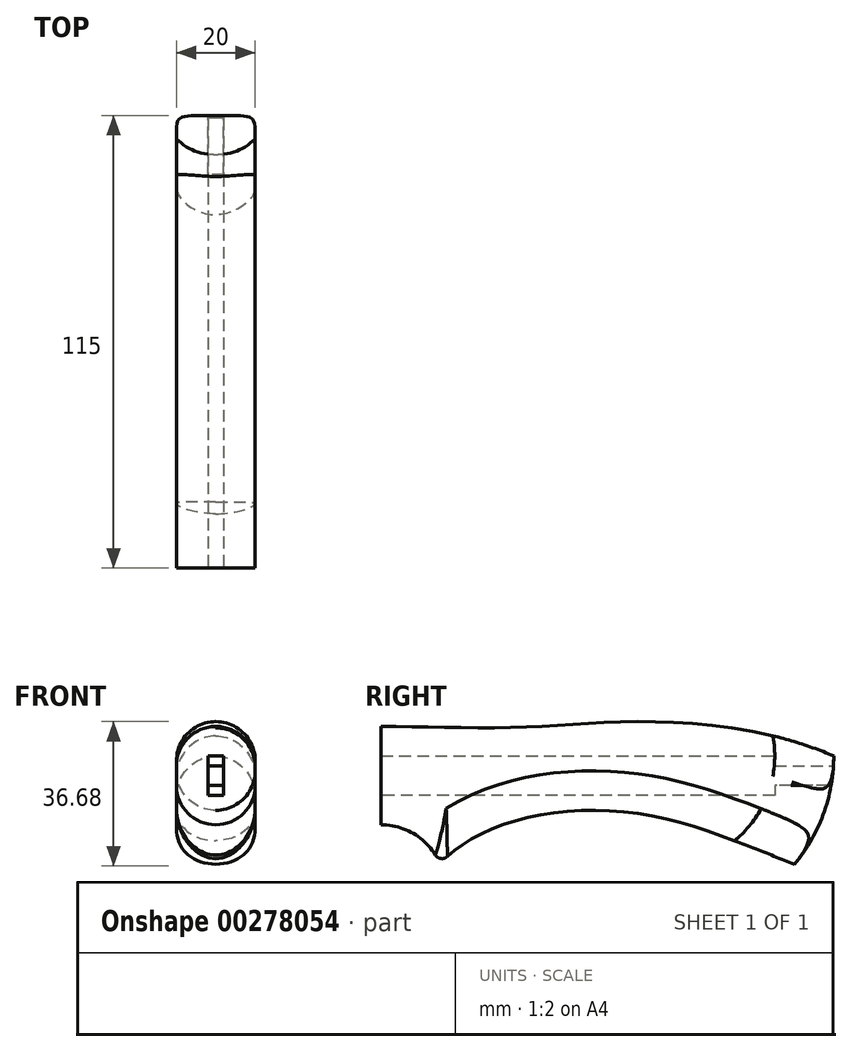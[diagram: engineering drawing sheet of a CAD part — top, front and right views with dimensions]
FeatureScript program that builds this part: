
annotation { "Feature Type Name" : "Feature", "Feature Type Description" : "" }
export const myFeature = defineFeature(function(context is Context, id is Id, definition is map)
    precondition{}
    {
        {
            var Q0;
            Q0=qCreatedBy(makeId("Right.planeOp"),FACE);
            var sketch = newSketch(context, id + "F0", { "sketchPlane" : qUnion([Q0])});
            skLineSegment(sketch, "E0", {"start": v(0, 0) * mm, "end": v(0, 5) * mm});
            skLineSegment(sketch, "E1", {"start": v(0, 5) * mm, "end": v(100, 5) * mm});
            skLineSegment(sketch, "E2", {"start": v(100, 5) * mm, "end": v(100, 2.5) * mm});
            skLineSegment(sketch, "E3", {"start": v(100, 2.5) * mm, "end": v(115, 2.5) * mm});
            skLineSegment(sketch, "E4", {"start": v(115, 2.5) * mm, "end": v(115, -2.5) * mm});
            skLineSegment(sketch, "E5", {"start": v(115, -2.5) * mm, "end": v(100, -2.5) * mm});
            skLineSegment(sketch, "E6", {"start": v(100, -2.5) * mm, "end": v(100, -5) * mm});
            skLineSegment(sketch, "E7", {"start": v(100, -5) * mm, "end": v(0, -5) * mm});
            skLineSegment(sketch, "E8", {"start": v(0, -5) * mm, "end": v(0, 0) * mm});
            skSolve(sketch);
        }
        {
            var Q0;
            Q0=qCreatedBy(makeId("Right.planeOp"),FACE);
            var sketch = newSketch(context, id + "F1", { "sketchPlane" : qUnion([Q0])});
            skLineSegment(sketch, "E9", {"start": v(0, 0) * mm, "end": v(0, 12.5) * mm});
            skLineSegment(sketch, "E10", {"start": v(0, 0) * mm, "end": v(0, -12.5) * mm});
            skLineSegment(sketch, "E11", {"start": v(0, -12.5) * mm, "end": v(-8.74, -12.5) * mm, "construction": true});
            skLineSegment(sketch, "E12", {"start": v(0, 12.5) * mm, "end": v(-9.37, 12.5) * mm, "construction": true});
            skFitSpline(sketch, "E13", {"points": [v(0, 12.5) * mm, v(33.17, 12.23) * mm, v(65.02, 13.71) * mm, v(115, 5) * mm], "startDerivative": vector(96.51, 0) * mm, "endDerivative": vector(135.83, -57.76) * mm});
            skArc(sketch, "E14", {"start": v(15, -22.5) * mm, "mid": v(9.01, -15.23) * mm, "end": v(0, -12.5) * mm});
            skArc(sketch, "E15", {"start": v(105, -22.5) * mm, "mid": v(112.42, -9.63) * mm, "end": v(115, 5) * mm});
            skLineSegment(sketch, "E16", {"start": v(115, 5) * mm, "end": v(115, 20.98) * mm, "construction": true});
            skFitSpline(sketch, "E17", {"points": [v(15, -22.5) * mm, v(32.94, -11.8) * mm, v(68.4, -10.16) * mm, v(105, -22.5) * mm], "startDerivative": vector(36.96, 44.62) * mm, "endDerivative": vector(92.76, -35.84) * mm});
            skArc(sketch, "E18", {"start": v(89.8, -16.52) * mm, "mid": v(98.31, -4.54) * mm, "end": v(99.53, 10.11) * mm});
            skSolve(sketch);
        }
        {
            var Q0;
            {var subQ2=sQuery(id+"F1.wireOp",EDGE,"E9");Q0=makeQuery(id+"F1.imprint","IMPRINT",FACE,{"disambiguationData":[TD([[makeQuery(id+"F1.imprint","IMPRINT",EDGE,{"derivedFrom":subQ2}),-1.0]])]});}
            extrude(context, id + "F2", {"entities" : qUnion([Q0]), "depth" : 10 * mm, "offsetDistance" : 25 * mm});
        }
        {
            var Q0;
            Q0=makeQuery(id+"F2.opExtrude","CAP_EDGE",EDGE,{"disambiguationData":[OSD([sQuery(id+"F1.wireOp",EDGE,"E13")])],"isStart":false});
            var Q1;
            Q1=makeQuery(id+"F2.opExtrude","CAP_EDGE",EDGE,{"disambiguationData":[OSD([sQuery(id+"F1.wireOp",EDGE,"E17")])],"isStart":false});
            var Q2;
            Q2=makeQuery(id+"F2.opExtrude","CAP_EDGE",EDGE,{"disambiguationData":[OSD([sQuery(id+"F1.wireOp",EDGE,"E14")])],"isStart":false});
            fillet(context, id + "F3", {"entities" : qUnion([Q0, Q1, Q2]), "tangentPropagation" : true, "radius" : 10 * mm, "defaultsChanged" : true, "vertexSettings" : [], "allowEdgeOverflow" : false});
        }
        {
            var Q0;
            {var subQ0=sQuery(id+"F1.wireOp",EDGE,"E15");Q0=makeQuery(id+"F1.imprint","IMPRINT",FACE,{"disambiguationData":[TD([[makeQuery(id+"F1.imprint","IMPRINT",EDGE,{"derivedFrom":subQ0}),1.0]])]});}
            extrude(context, id + "F4", {"entities" : qUnion([Q0]), "depth" : 10 * mm, "offsetDistance" : 25 * mm});
        }
        {
            var Q0;
            Q0=makeQuery(id+"F4.opExtrude","CAP_EDGE",EDGE,{"disambiguationData":[OSD([sQuery(id+"F1.wireOp",EDGE,"E13")])],"isStart":false});
            var Q1;
            Q1=makeQuery(id+"F4.opExtrude","CAP_EDGE",EDGE,{"disambiguationData":[OSD([sQuery(id+"F1.wireOp",EDGE,"E17")])],"isStart":false});
            fillet(context, id + "F5", {"entities" : qUnion([Q0, Q1]), "tangentPropagation" : true, "radius" : 10 * mm, "defaultsChanged" : true, "vertexSettings" : [], "allowEdgeOverflow" : false});
        }
        {
            var Q0;
            Q0=makeQuery(id+"F4.opExtrude","CAP_EDGE",EDGE,{"disambiguationData":[OSD([sQuery(id+"F1.wireOp",EDGE,"E15")])],"isStart":false});
            fillet(context, id + "F6", {"entities" : qUnion([Q0]), "tangentPropagation" : true, "crossSection" : FilletCrossSection.CURVATURE, "radius" : 10 * mm, "magnitude" : 0.9, "defaultsChanged" : true, "vertexSettings" : []});
        }
        {
            var Q0;
            Q0=makeQuery(id+"F0.imprint","IMPRINT",FACE,{"disambiguationData":[TD([[makeQuery(id+"F0.imprint","IMPRINT",EDGE,{"derivedFrom":sQuery(id+"F0.wireOp",EDGE,"E0")}),-1.0]])]});
            extrude(context, id + "F7", {"entities" : qUnion([Q0]), "operationType" : NewBodyOperationType.REMOVE, "depth" : 2 * mm, "offsetDistance" : 25 * mm});
        }
        {
            var Q0;
            Q0=makeQuery(id+"F2.opExtrude","SWEPT_BODY",BODY,{"disambiguationData":[OSD([sQuery(id+"F1.wireOp",EDGE,"E9"),sQuery(id+"F1.wireOp",EDGE,"E10"),sQuery(id+"F1.wireOp",EDGE,"E13"),sQuery(id+"F1.wireOp",EDGE,"E14"),sQuery(id+"F1.wireOp",EDGE,"E17"),sQuery(id+"F1.wireOp",EDGE,"E18")])]});
            var Q1;
            Q1=qCreatedBy(makeId("Right.planeOp"),FACE);
            mirror(context, id + "F8", {"operationType" : NewBodyOperationType.ADD, "entities" : qUnion([Q0]), "mirrorPlane" : qUnion([Q1])});
        }
        {
            var Q0;
            Q0=makeQuery(id+"F4.opExtrude","SWEPT_BODY",BODY,{"disambiguationData":[OSD([sQuery(id+"F1.wireOp",EDGE,"E13"),sQuery(id+"F1.wireOp",EDGE,"E15"),sQuery(id+"F1.wireOp",EDGE,"E17"),sQuery(id+"F1.wireOp",EDGE,"E18")])]});
            var Q1;
            Q1=qCreatedBy(makeId("Right.planeOp"),FACE);
            mirror(context, id + "F9", {"operationType" : NewBodyOperationType.ADD, "entities" : qUnion([Q0]), "mirrorPlane" : qUnion([Q1])});
        }
        {
            var Q0;
            Q0=makeQuery(id+"F8.opPattern","COPY",EDGE,{"derivedFrom":makeQuery(id+"F3.opFillet","BLEND_EDGE",EDGE,{"blendedFrom":[makeQuery(id+"F2.opExtrude","CAP_EDGE",EDGE,{"disambiguationData":[OSD([sQuery(id+"F1.wireOp",EDGE,"E14")])],"isStart":false}),makeQuery(id+"F2.opExtrude","CAP_EDGE",EDGE,{"disambiguationData":[OSD([sQuery(id+"F1.wireOp",EDGE,"E17")])],"isStart":false})],"blendedInto":[]}),"instanceName":"1"});
            fillet(context, id + "F10", {"entities" : qUnion([Q0]), "tangentPropagation" : true, "radius" : 2 * mm, "defaultsChanged" : true, "vertexSettings" : [], "allowEdgeOverflow" : false});
        }
    });
